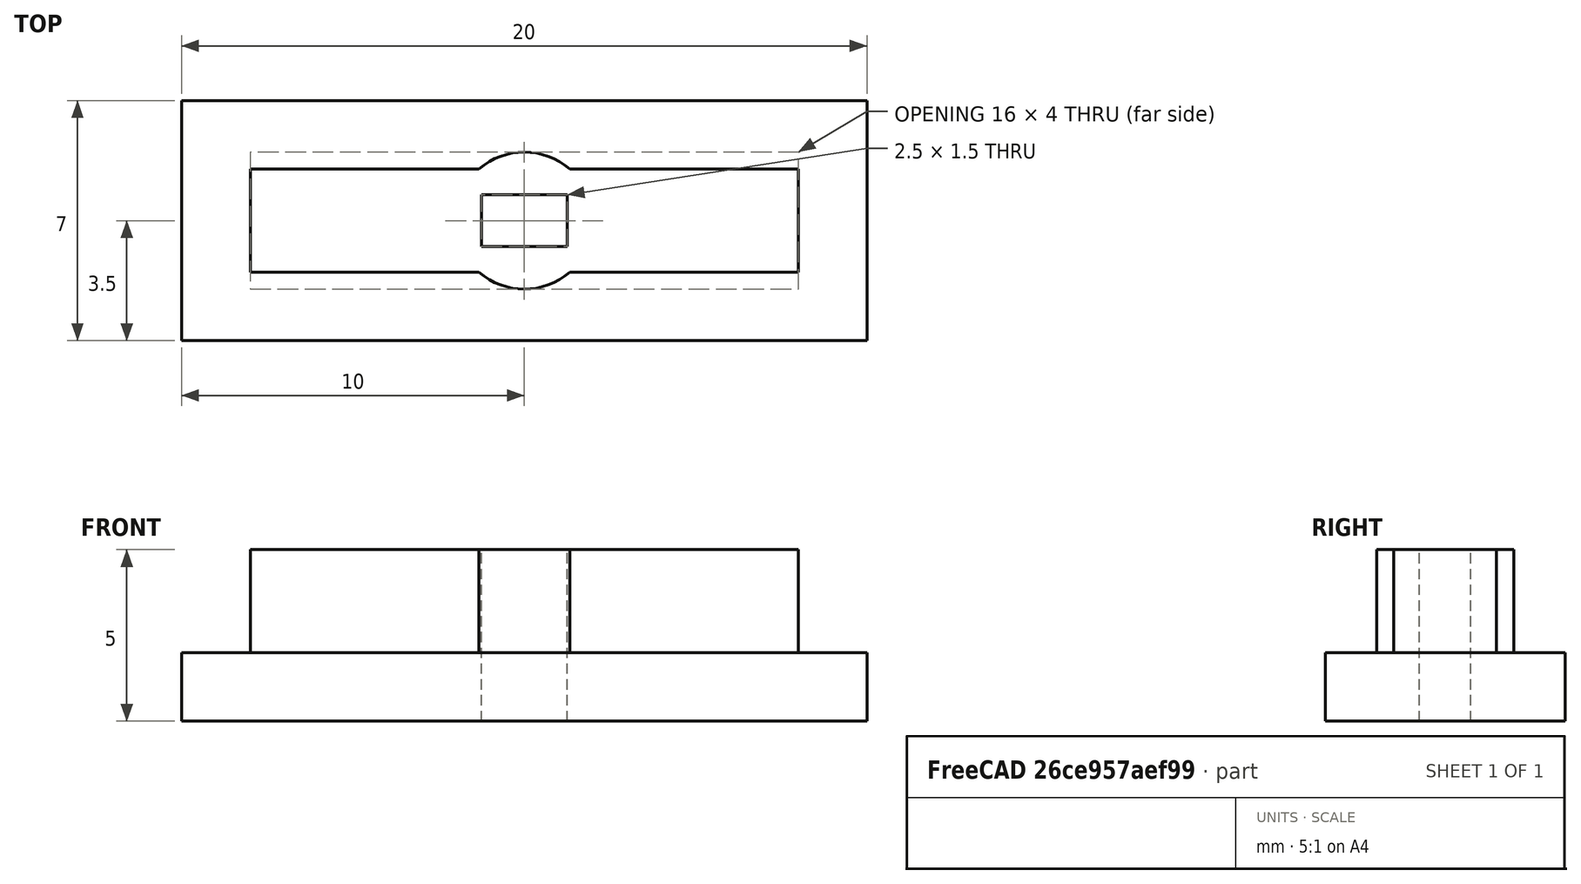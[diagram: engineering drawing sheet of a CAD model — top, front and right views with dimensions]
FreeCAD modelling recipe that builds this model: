
FCSTD DOCUMENT  (FreeCAD 0.16R6707 (Git))
Label: xmaxx-closure
License: All rights reserved
LicenseURL: http://en.wikipedia.org/wiki/All_rights_reserved
objects: Part::Box×3, Part::MultiFuse×2, Part::Cylinder×1, Part::Cut×1
note: 7 computed .brp shape members not serialized (recipe doc carries the construction recipe); baked Part::Feature solids carry a one-line shape summary decoded from their .brp

FEATURE [Part::Cylinder] Cylinder
  Angle = 360
  Height = 5
  Radius = 2
FEATURE [Part::Box] Box  label="Cube"
  Height = 5
  Length = 16
  Placement = pos=(-8,-1.5,0) rot=(0,0,1;0rad)
  Width = 3
FEATURE [Part::Box] Box001  label="Cube001"
  Height = 10
  Length = 2.5
  Placement = pos=(-1.25,-0.75,0) rot=(0,0,1;0rad)
  Width = 1.5
FEATURE [Part::MultiFuse] Fusion
  Shapes = -> [Cylinder,Box]
FEATURE [Part::Box] Box002  label="Cube002"
  Height = 2
  Length = 20
  Placement = pos=(-10,-3.5,0) rot=(0,0,1;0rad)
  Width = 7
FEATURE [Part::MultiFuse] Fusion001
  Shapes = -> [Box002,Fusion]
FEATURE [Part::Cut] Cut
  Base = -> Fusion001
  Tool = -> Box001
